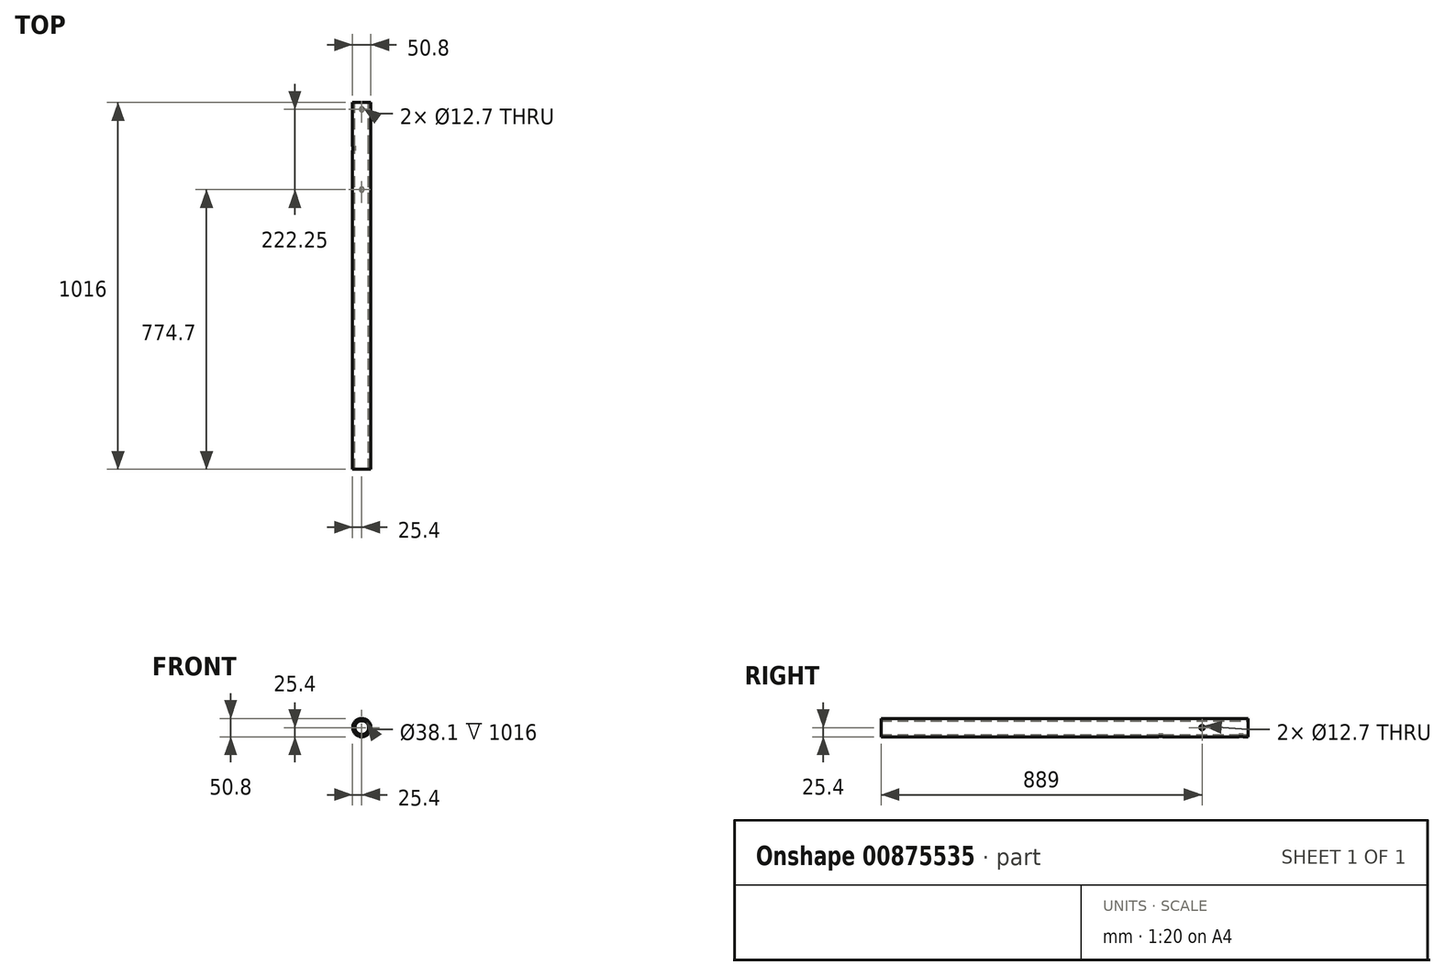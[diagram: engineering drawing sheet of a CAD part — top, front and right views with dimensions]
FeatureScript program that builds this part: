
annotation { "Feature Type Name" : "Feature", "Feature Type Description" : "" }
export const myFeature = defineFeature(function(context is Context, id is Id, definition is map)
    precondition{}
    {
        {
            var Q0;
            Q0=qCreatedBy(makeId("Front.planeOp"),FACE);
            var sketch = newSketch(context, id + "F0", { "sketchPlane" : qUnion([Q0])});
            skCircle(sketch, "E0", {"center": v(0, 0) * mm, "radius": 25.4 * mm});
            skCircle(sketch, "E1", {"center": v(0, 0) * mm, "radius": 19.05 * mm});
            skSolve(sketch);
        }
        {
            var Q0;
            Q0=makeQuery(id+"F0.imprint","IMPRINT",FACE,{"disambiguationData":[TD([[makeQuery(id+"F0.imprint","IMPRINT",EDGE,{"derivedFrom":sQuery(id+"F0.wireOp",EDGE,"E0")}),1.0]])]});
            extrude(context, id + "F1", {"entities" : qUnion([Q0]), "endBound" : BoundingType.SYMMETRIC, "depth" : 1016 * mm, "offsetDistance" : 25.4 * mm});
        }
        {
            var Q0;
            Q0=makeQuery(id+"F1.opExtrude","CAP_FACE",FACE,{"disambiguationData":[OSD([sQuery(id+"F0.wireOp",EDGE,"E0"),sQuery(id+"F0.wireOp",EDGE,"E1")])],"isStart":true});
            var sketch = newSketch(context, id + "F2", { "sketchPlane" : qUnion([Q0])});
            skLineSegment(sketch, "E2", {"start": v(0, -25.4) * mm, "end": v(0, 0) * mm});
            skLineSegment(sketch, "E3", {"start": v(0, 0) * mm, "end": v(-25.4, 0) * mm});
            skLineSegment(sketch, "E4", {"start": v(25.4, 0) * mm, "end": v(0, 0) * mm});
            skSolve(sketch);
        }
        {
            var Q0;
            Q0=qCreatedBy(makeId("Right.planeOp"),FACE);
            var sketch = newSketch(context, id + "F3", { "sketchPlane" : qUnion([Q0])});
            skLineSegment(sketch, "E5", {"start": v(0, 0) * mm, "end": v(0, -25.4) * mm});
            skLineSegment(sketch, "E6", {"start": v(0, -25.4) * mm, "end": v(508, -25.4) * mm});
            skCircle(sketch, "E7", {"center": v(381, 0) * mm, "radius": 6.35 * mm});
            skSolve(sketch);
        }
        {
            var Q0;
            Q0=qCreatedBy(makeId("Top.planeOp"),FACE);
            var sketch = newSketch(context, id + "F4", { "sketchPlane" : qUnion([Q0])});
            skLineSegment(sketch, "E8", {"start": v(0, 0) * mm, "end": v(25.4, 0) * mm});
            skLineSegment(sketch, "E9", {"start": v(0, 0) * mm, "end": v(-25.4, 0) * mm});
            skLineSegment(sketch, "E10", {"start": v(-25.4, 0) * mm, "end": v(-25.4, 508) * mm});
            skLineSegment(sketch, "E11", {"start": v(25.4, 0) * mm, "end": v(25.4, 508) * mm});
            skCircle(sketch, "E12", {"center": v(0, 488.95) * mm, "radius": 6.35 * mm});
            skCircle(sketch, "E13", {"center": v(0, 266.7) * mm, "radius": 6.35 * mm});
            skSolve(sketch);
        }
        {
            var Q0;
            Q0 = qSketchRegion(id + "F4", true);
            extrude(context, id + "F5", {"entities" : qUnion([Q0]), "operationType" : NewBodyOperationType.REMOVE, "oppositeDirection" : true, "depth" : 25.4 * mm, "offsetDistance" : 25.4 * mm});
        }
        {
            var Q0;
            Q0 = qSketchRegion(id + "F3", true);
            extrude(context, id + "F6", {"entities" : qUnion([Q0]), "operationType" : NewBodyOperationType.REMOVE, "endBound" : BoundingType.SYMMETRIC, "depth" : 50.8 * mm, "offsetDistance" : 25.4 * mm});
        }
    });
